# Revit family: Fireplace_Wood_Heatilator_Constitution
name_source: partatom
category: Mechanical Equipment
revit_build: Autodesk Revit 2015 (Build: 20140323_1530(x64)
units: mm (PartAtom-declared; Revit-internal decimal feet)

## types (3) — shared parameters
Assembly Code = D3020
Default Elevation = 0' - 0"
Description = Heatilator Woodburning Fireplace - Constitution as Specified
Efficiency Ratings = Steady State 77.8%
Electrical_Voltage = 120 V
Fixture Finish = Metal - HeatNGlo - Metallic Black
Fuel Consumption = as Specified
Fuel Type = Cord Wood
HVAC_BTU Output = 51000.0 Btu/h
Heating Capacity = 2600 sq ft
Keynote = 10305
Manufacturer = Heatilator
Manufacturer Website = http://www.heatilator.com
Opening Height = 2' - 7 1/8"
Opening Width = 3' - 1"
Product Data = http://www.arcat.com
Revision = R1_04_2014
Sales Information = http://www.heatilator.com
Send Message = http://www.arcat.com
Standards Conformance = EPA Certified
URL = http://www.heatilator.com
Unit Depth = 2' - 0 1/8"
Unit Height = 3' - 7 3/4"
Unit Weight = 650
Unit Width = 3' - 6"
zero-valued in all types: Expected Lifespan (Years), Maintenance Schedule (Months), Warranty Duration (Years)

## type names (no varying parameters)
- CONSTITUTION-NT
- CONSTITUTION-GT
- CONSTITUTION-BK

note: column(s) folded — value = type name in every type: Model

## geometry (parser evidence)
native form markers: Blend x2, Sweep x3
no freeform markers — native parametric forms only
